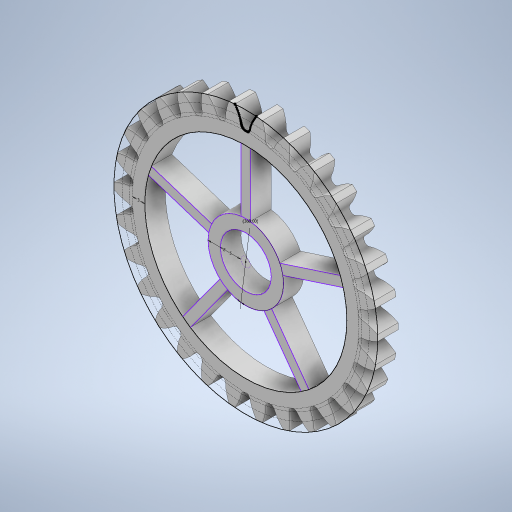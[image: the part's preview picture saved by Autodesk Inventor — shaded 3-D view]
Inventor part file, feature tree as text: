
AUTODESK INVENTOR PART (.ipt)
format: ipt  version: 2023 (Build 270158000, 158)  size: 514,560 bytes
history: native  units: mm
features: extrude x3, pattern_circular x1
ambient origin geometry x8: Origin, YZ Plane, XZ Plane, XY Plane, X Axis, Y Axis, Z Axis, Center Point
bodies: Solid1 (feature_tree)
feature tree (4):
  extrude  "Extrusion1"  Depth=5.0mm
  extrude  "Extrusion2"  TaperAngle=0.0deg  [1 undecoded]
  extrude  "Extrusion3"  Depth=3.0mm
  pattern_circular  "Circular Pattern1"  [2 undecoded]
note: 3 required parameter values undecoded (feature->parameter linkage not recoverable at this tier; creation-order binding heuristic only, values carry confidence <= 0.55)
